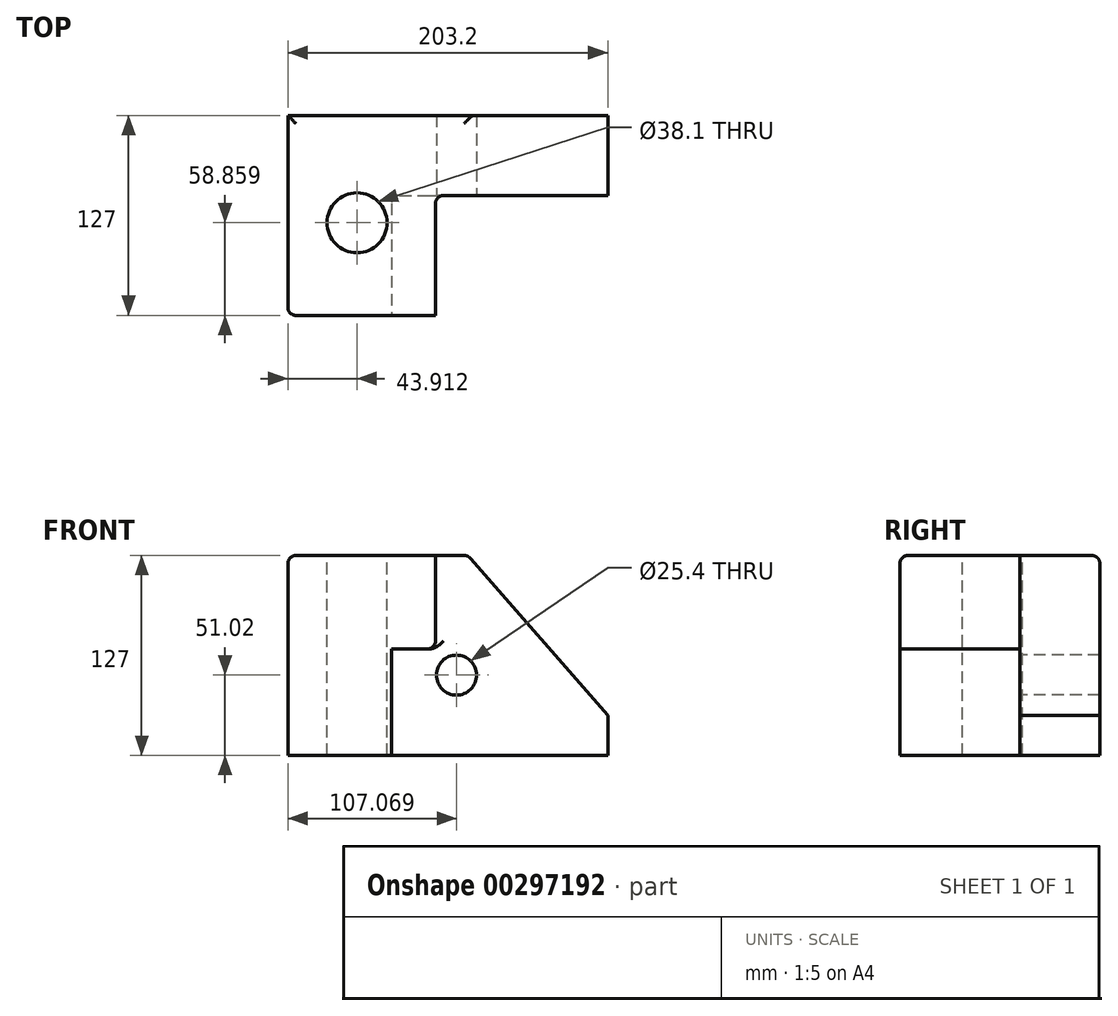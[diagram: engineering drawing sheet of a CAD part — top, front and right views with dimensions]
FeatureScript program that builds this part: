
annotation { "Feature Type Name" : "Feature", "Feature Type Description" : "" }
export const myFeature = defineFeature(function(context is Context, id is Id, definition is map)
    precondition{}
    {
        {
            var Q0;
            Q0=qCreatedBy(makeId("Front.planeOp"),FACE);
            var sketch = newSketch(context, id + "F0", { "sketchPlane" : qUnion([Q0])});
            skLineSegment(sketch, "E0.bottom", {"start": v(-87.98, 71.81) * mm, "end": v(115.22, 71.81) * mm});
            skLineSegment(sketch, "E0.top", {"start": v(-87.98, -55.19) * mm, "end": v(115.22, -55.19) * mm});
            skLineSegment(sketch, "E0.left", {"start": v(-87.98, 71.81) * mm, "end": v(-87.98, -55.19) * mm});
            skLineSegment(sketch, "E0.right", {"start": v(115.22, 71.81) * mm, "end": v(115.22, -55.19) * mm});
            skSolve(sketch);
        }
        {
            var Q0;
            Q0=makeQuery(id+"F0.imprint","IMPRINT",FACE,{"disambiguationData":[TD([[makeQuery(id+"F0.imprint","IMPRINT",EDGE,{"derivedFrom":sQuery(id+"F0.wireOp",EDGE,"E0.bottom")}),-1.0]])]});
            extrude(context, id + "F1", {"entities" : qUnion([Q0]), "depth" : 127 * mm});
        }
        {
            var Q0;
            Q0=makeQuery(id+"F1.opExtrude","CAP_FACE",FACE,{"disambiguationData":[OSD([sQuery(id+"F0.wireOp",EDGE,"E0.bottom"),sQuery(id+"F0.wireOp",EDGE,"E0.top"),sQuery(id+"F0.wireOp",EDGE,"E0.left"),sQuery(id+"F0.wireOp",EDGE,"E0.right")])],"isStart":false});
            var sketch = newSketch(context, id + "F2", { "sketchPlane" : qUnion([Q0])});
            skLineSegment(sketch, "E1", {"start": v(-87.98, 71.81) * mm, "end": v(-87.98, -55.19) * mm});
            skLineSegment(sketch, "E2", {"start": v(-87.98, -55.19) * mm, "end": v(-22.09, -55.19) * mm});
            skLineSegment(sketch, "E3", {"start": v(-22.09, -55.19) * mm, "end": v(-22.09, 12.5) * mm});
            skLineSegment(sketch, "E4", {"start": v(-22.09, 12.5) * mm, "end": v(5.8, 12.5) * mm});
            skLineSegment(sketch, "E5", {"start": v(5.8, 12.5) * mm, "end": v(5.8, 71.81) * mm});
            skLineSegment(sketch, "E6", {"start": v(5.8, 71.81) * mm, "end": v(-87.98, 71.81) * mm});
            skSolve(sketch);
        }
        {
            var Q0;
            {var subQ3=sQuery(id+"F2.wireOp",EDGE,"E3");Q0=makeQuery(id+"F2.imprint","IMPRINT",FACE,{"disambiguationData":[TD([[makeQuery(id+"F2.imprint","IMPRINT",EDGE,{"derivedFrom":subQ3}),-1.0]])]});}
            extrude(context, id + "F3", {"entities" : qUnion([Q0]), "operationType" : NewBodyOperationType.REMOVE, "oppositeDirection" : true, "depth" : 76.2 * mm});
        }
        {
            var Q0;
            Q0=makeQuery(id+"F1.opExtrude","SWEPT_EDGE",EDGE,{"disambiguationData":[OSD([sQuery(id+"F0.wireOp",EDGE,"E0.bottom"),sQuery(id+"F0.wireOp",EDGE,"E0.right")])]});
            chamfer(context, id + "F4", {"entities" : qUnion([Q0]), "chamferType" : ChamferType.TWO_OFFSETS, "width1" : 88.9 * mm, "oppositeDirection" : false, "width2" : 101.6 * mm, "tangentPropagation" : true});
        }
        {
            var Q0;
            Q0=makeQuery(id+"F3.boolean.opBoolean","COPY",EDGE,{"derivedFrom":makeQuery(id+"F3.opExtrude","CAP_EDGE",EDGE,{"disambiguationData":[OSD([sQuery(id+"F2.wireOp",EDGE,"E5")])],"isStart":false})});
            var Q1;
            Q1=makeQuery(id+"F3.boolean.opBoolean","COPY",EDGE,{"derivedFrom":makeQuery(id+"F3.opExtrude","SWEPT_EDGE",EDGE,{"disambiguationData":[OSD([sQuery(id+"F0.wireOp",EDGE,"E0.bottom"),sQuery(id+"F2.wireOp",EDGE,"E5"),sQuery(id+"F2.wireOp",EDGE,"E6")])]})});
            var Q2;
            Q2=makeQuery(id+"F3.boolean.opBoolean","COPY",EDGE,{"derivedFrom":makeQuery(id+"F3.opExtrude","CAP_EDGE",EDGE,{"disambiguationData":[OSD([sQuery(id+"F2.wireOp",EDGE,"E5")])],"isStart":true})});
            var Q3;
            {var subQ0=sQuery(id+"F0.wireOp",EDGE,"E0.bottom");Q3=makeQuery(id+"F4.opChamfer","BLEND_EDGE",EDGE,{"blendedFrom":[makeQuery(id+"F1.opExtrude","SWEPT_EDGE",EDGE,{"disambiguationData":[OSD([subQ0,sQuery(id+"F0.wireOp",EDGE,"E0.right")])]}),makeQuery(id+"F1.opExtrude","SWEPT_FACE",FACE,{"disambiguationData":[OSD([subQ0])]})],"blendedInto":[makeQuery(id+"F1.opExtrude","SWEPT_FACE",FACE,{"disambiguationData":[OSD([subQ0])]})]});}
            var Q4;
            Q4=makeQuery(id+"F1.opExtrude","CAP_EDGE",EDGE,{"disambiguationData":[OSD([sQuery(id+"F0.wireOp",EDGE,"E0.bottom")])],"isStart":true});
            var Q5;
            Q5=makeQuery(id+"F1.opExtrude","SWEPT_EDGE",EDGE,{"disambiguationData":[OSD([sQuery(id+"F0.wireOp",EDGE,"E0.bottom"),sQuery(id+"F0.wireOp",EDGE,"E0.left")])]});
            var Q6;
            Q6=makeQuery(id+"F3.boolean.opBoolean","COPY",EDGE,{"derivedFrom":makeQuery(id+"F3.opExtrude","CAP_EDGE",EDGE,{"disambiguationData":[OSD([sQuery(id+"F2.wireOp",EDGE,"E4")])],"isStart":true})});
            var Q7;
            Q7=makeQuery(id+"F3.boolean.opBoolean","COPY",EDGE,{"derivedFrom":makeQuery(id+"F3.opExtrude","CAP_EDGE",EDGE,{"disambiguationData":[OSD([sQuery(id+"F2.wireOp",EDGE,"E3")])],"isStart":false})});
            var Q8;
            Q8=makeQuery(id+"F3.boolean.opBoolean","COPY",EDGE,{"derivedFrom":makeQuery(id+"F3.opExtrude","CAP_EDGE",EDGE,{"disambiguationData":[OSD([sQuery(id+"F2.wireOp",EDGE,"E3")])],"isStart":true})});
            var Q9;
            Q9=makeQuery(id+"F1.opExtrude","CAP_EDGE",EDGE,{"disambiguationData":[OSD([sQuery(id+"F0.wireOp",EDGE,"E0.left")])],"isStart":false});
            var Q10;
            Q10=makeQuery(id+"F1.opExtrude","CAP_EDGE",EDGE,{"disambiguationData":[OSD([sQuery(id+"F0.wireOp",EDGE,"E0.bottom")])],"isStart":false});
            fillet(context, id + "F5", {"entities" : qUnion([Q0, Q1, Q2, Q3, Q4, Q5, Q6, Q7, Q8, Q9, Q10]), "radius" : 5.08 * mm, "tangentPropagation" : true, "allowEdgeOverflow" : false});
        }
        {
            var Q0;
            Q0=makeQuery(id+"F5.opFillet","BLEND_EDGE",EDGE,{"blendedFrom":[makeQuery(id+"F3.boolean.opBoolean","COPY",EDGE,{"derivedFrom":makeQuery(id+"F3.opExtrude","CAP_EDGE",EDGE,{"disambiguationData":[OSD([sQuery(id+"F2.wireOp",EDGE,"E5")])],"isStart":false})}),makeQuery(id+"F3.boolean.opBoolean","COPY",FACE,{"derivedFrom":makeQuery(id+"F3.opExtrude","SWEPT_FACE",FACE,{"disambiguationData":[OSD([sQuery(id+"F2.wireOp",EDGE,"E4")])]})})],"blendedInto":[makeQuery(id+"F3.boolean.opBoolean","COPY",FACE,{"derivedFrom":makeQuery(id+"F3.opExtrude","SWEPT_FACE",FACE,{"disambiguationData":[OSD([sQuery(id+"F2.wireOp",EDGE,"E4")])]})})]});
            fillet(context, id + "F6", {"entities" : qUnion([Q0]), "radius" : 5.08 * mm, "tangentPropagation" : true, "allowEdgeOverflow" : false});
        }
        {
            var Q0;
            Q0=makeQuery(id+"F3.boolean.opBoolean","COPY",FACE,{"derivedFrom":makeQuery(id+"F3.opExtrude","CAP_FACE",FACE,{"disambiguationData":[OSD([sQuery(id+"F0.wireOp",EDGE,"E0.bottom"),sQuery(id+"F0.wireOp",EDGE,"E0.top"),sQuery(id+"F0.wireOp",EDGE,"E0.right"),sQuery(id+"F2.wireOp",EDGE,"E3"),sQuery(id+"F2.wireOp",EDGE,"E4"),sQuery(id+"F2.wireOp",EDGE,"E5")])],"isStart":false})});
            var sketch = newSketch(context, id + "F7", { "sketchPlane" : qUnion([Q0])});
            skCircle(sketch, "E7", {"center": v(19.09, -4.17) * mm, "radius": 12.7 * mm});
            skSolve(sketch);
        }
        {
            var Q0;
            Q0=makeQuery(id+"F7.imprint","IMPRINT",FACE,{"disambiguationData":[TD([[makeQuery(id+"F7.imprint","IMPRINT",EDGE,{"derivedFrom":sQuery(id+"F7.wireOp",EDGE,"E7")}),1.0]])]});
            extrude(context, id + "F8", {"entities" : qUnion([Q0]), "operationType" : NewBodyOperationType.REMOVE, "endBound" : BoundingType.THROUGH_ALL, "oppositeDirection" : true, "depth" : 25.4 * mm});
        }
        {
            var Q0;
            Q0=makeQuery(id+"F1.opExtrude","SWEPT_FACE",FACE,{"disambiguationData":[OSD([sQuery(id+"F0.wireOp",EDGE,"E0.bottom")])]});
            var sketch = newSketch(context, id + "F9", { "sketchPlane" : qUnion([Q0])});
            skCircle(sketch, "E8", {"center": v(-44.07, -68.14) * mm, "radius": 19.05 * mm});
            skSolve(sketch);
        }
        {
            var Q0;
            Q0=makeQuery(id+"F9.imprint","IMPRINT",FACE,{"disambiguationData":[TD([[makeQuery(id+"F9.imprint","IMPRINT",EDGE,{"derivedFrom":sQuery(id+"F9.wireOp",EDGE,"E8")}),1.0]])]});
            extrude(context, id + "F10", {"entities" : qUnion([Q0]), "operationType" : NewBodyOperationType.REMOVE, "endBound" : BoundingType.THROUGH_ALL, "oppositeDirection" : true, "depth" : 25.4 * mm});
        }
    });
